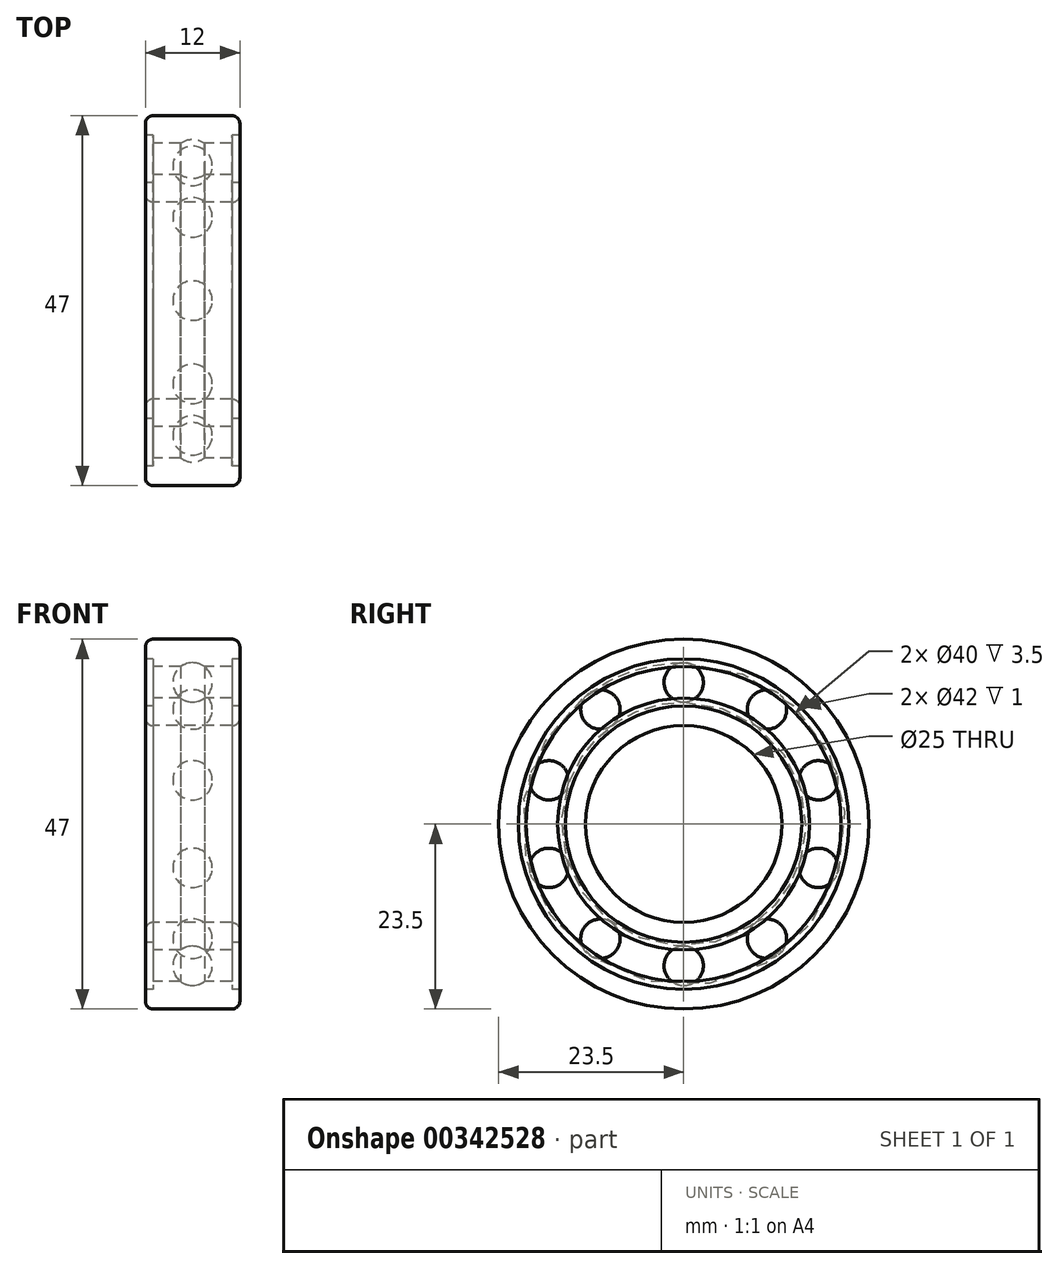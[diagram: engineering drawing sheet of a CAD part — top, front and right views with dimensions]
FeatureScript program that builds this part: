
annotation { "Feature Type Name" : "Feature", "Feature Type Description" : "" }
export const myFeature = defineFeature(function(context is Context, id is Id, definition is map)
    precondition{}
    {
        {
            var Q0;
            Q0=qCreatedBy(makeId("Front.planeOp"),FACE);
            var sketch = newSketch(context, id + "F0", { "sketchPlane" : qUnion([Q0])});
            skLineSegment(sketch, "E0", {"start": v(-19.95, 0) * mm, "end": v(21.28, 0) * mm});
            skLineSegment(sketch, "E1", {"start": v(0, 12.5) * mm, "end": v(5, 12.5) * mm});
            skLineSegment(sketch, "E2", {"start": v(6, 13.5) * mm, "end": v(6, 15) * mm});
            skLineSegment(sketch, "E3", {"start": v(6, 15) * mm, "end": v(5, 15) * mm});
            skLineSegment(sketch, "E4.MirrorCS", {"start": v(-6, 15) * mm, "end": v(-5, 15) * mm});
            skLineSegment(sketch, "E5.MirrorCS", {"start": v(-6, 13.5) * mm, "end": v(-6, 15) * mm});
            skLineSegment(sketch, "E6.MirrorCS", {"start": v(0, 12.5) * mm, "end": v(-5, 12.5) * mm});
            skPoint(sketch, "E7.visualSharp", {"position": v(-6, 12.5) * mm});
            skArc(sketch, "E7.filletArc", {"start": v(-6, 13.5) * mm, "mid": v(-5.7, 12.8) * mm, "end": v(-5, 12.5) * mm});
            skPoint(sketch, "E8.visualSharp", {"position": v(6, 12.5) * mm});
            skArc(sketch, "E8.filletArc", {"start": v(5, 12.5) * mm, "mid": v(5.7, 12.8) * mm, "end": v(6, 13.5) * mm});
            skLineSegment(sketch, "E9", {"start": v(6, 21) * mm, "end": v(5, 21) * mm});
            skLineSegment(sketch, "E10", {"start": v(0, 23.5) * mm, "end": v(5, 23.5) * mm});
            skLineSegment(sketch, "E11", {"start": v(6, 22.5) * mm, "end": v(6, 21) * mm});
            skPoint(sketch, "E12.visualSharp", {"position": v(6, 23.5) * mm});
            skArc(sketch, "E12.filletArc", {"start": v(6, 22.5) * mm, "mid": v(5.7, 23.2) * mm, "end": v(5, 23.5) * mm});
            skArc(sketch, "E13.MirrorCS", {"start": v(-6, 22.5) * mm, "mid": v(-5.7, 23.2) * mm, "end": v(-5, 23.5) * mm});
            skLineSegment(sketch, "E14.MirrorCS", {"start": v(-6, 22.5) * mm, "end": v(-6, 21) * mm});
            skLineSegment(sketch, "E15.MirrorCS", {"start": v(-6, 21) * mm, "end": v(-5, 21) * mm});
            skPoint(sketch, "E16.MirrorP", {"position": v(-6, 23.5) * mm});
            skLineSegment(sketch, "E17.MirrorCS", {"start": v(0, 23.5) * mm, "end": v(-5, 23.5) * mm});
            skLineSegment(sketch, "E18", {"start": v(-5, 21) * mm, "end": v(-5, 20) * mm});
            skLineSegment(sketch, "E19", {"start": v(-5, 20) * mm, "end": v(-1.5, 20) * mm});
            skLineSegment(sketch, "E20", {"start": v(5, 20) * mm, "end": v(5, 20.54) * mm});
            skLineSegment(sketch, "E21", {"start": v(-5, 15) * mm, "end": v(-5, 16) * mm});
            skLineSegment(sketch, "E22", {"start": v(-5, 16) * mm, "end": v(-1.5, 16) * mm});
            skLineSegment(sketch, "E23", {"start": v(5, 16) * mm, "end": v(5, 15) * mm});
            skArc(sketch, "E24", {"start": v(-1.5, 16) * mm, "mid": v(0, 15.5) * mm, "end": v(1.5, 16) * mm});
            skArc(sketch, "E25.trimOffspring", {"start": v(1.5, 20) * mm, "mid": v(0, 20.5) * mm, "end": v(-1.5, 20) * mm});
            skLineSegment(sketch, "E26.trimOffspring", {"start": v(1.5, 20) * mm, "end": v(5, 20) * mm});
            skPoint(sketch, "E27.orphan", {"position": v(0, 20) * mm});
            skPoint(sketch, "E28.end.orphan", {"position": v(0, 16) * mm});
            skLineSegment(sketch, "E29.trimOffspring", {"start": v(1.5, 16) * mm, "end": v(5, 16) * mm});
            skLineSegment(sketch, "E30", {"start": v(5, 20.54) * mm, "end": v(5, 21) * mm});
            skArc(sketch, "E31", {"start": v(-1.5, 16) * mm, "mid": v(2.5, 18) * mm, "end": v(-1.5, 20) * mm});
            skLineSegment(sketch, "E32", {"start": v(0, 20.5) * mm, "end": v(0, 15.5) * mm});
            skSolve(sketch);
        }
        {
            var Q0;
            Q0=makeQuery(id+"F0.imprint","IMPRINT",FACE,{"disambiguationData":[TD([[makeQuery(id+"F0.imprint","IMPRINT",EDGE,{"derivedFrom":sQuery(id+"F0.wireOp",EDGE,"E9")}),-1.0]])]});
            var Q1;
            Q1=makeQuery(id+"F0.imprint","IMPRINT",FACE,{"disambiguationData":[TD([[makeQuery(id+"F0.imprint","IMPRINT",EDGE,{"derivedFrom":sQuery(id+"F0.wireOp",EDGE,"E1")}),1.0]])]});
            var Q2;
            Q2=sQuery(id+"F0.wireOp",EDGE,"E0");
            revolve(context, id + "F1", {"entities" : qUnion([Q0, Q1]), "axis" : qUnion([Q2]), "revolveType" : RevolveType.FULL});
        }
        {
            var Q0;
            {var subQ2=sQuery(id+"F0.wireOp",EDGE,"E32");Q0=makeQuery(id+"F0.imprint","IMPRINT",FACE,{"disambiguationData":[TD([[makeQuery(id+"F0.imprint","IMPRINT",EDGE,{"derivedFrom":subQ2}),1.0]])]});}
            var Q1;
            Q1=sQuery(id+"F0.wireOp",EDGE,"E32");
            revolve(context, id + "F2", {"entities" : qUnion([Q0]), "axis" : qUnion([Q1]), "revolveType" : RevolveType.FULL});
        }
        {
            var Q0;
            Q0=makeQuery(id+"F2.opRevolve","SWEPT_BODY",BODY,{"disambiguationData":[OSD([sQuery(id+"F0.wireOp",EDGE,"E31"),sQuery(id+"F0.wireOp",EDGE,"E32")])]});
            var Q1;
            Q1=sQuery(id+"F0.wireOp",EDGE,"E0");
            circularPattern(context, id + "F3", {"entities" : qUnion([Q0]), "axis" : qUnion([Q1]), "angle" : 360 * degree, "instanceCount" : 10, "equalSpace" : true});
        }
    });
